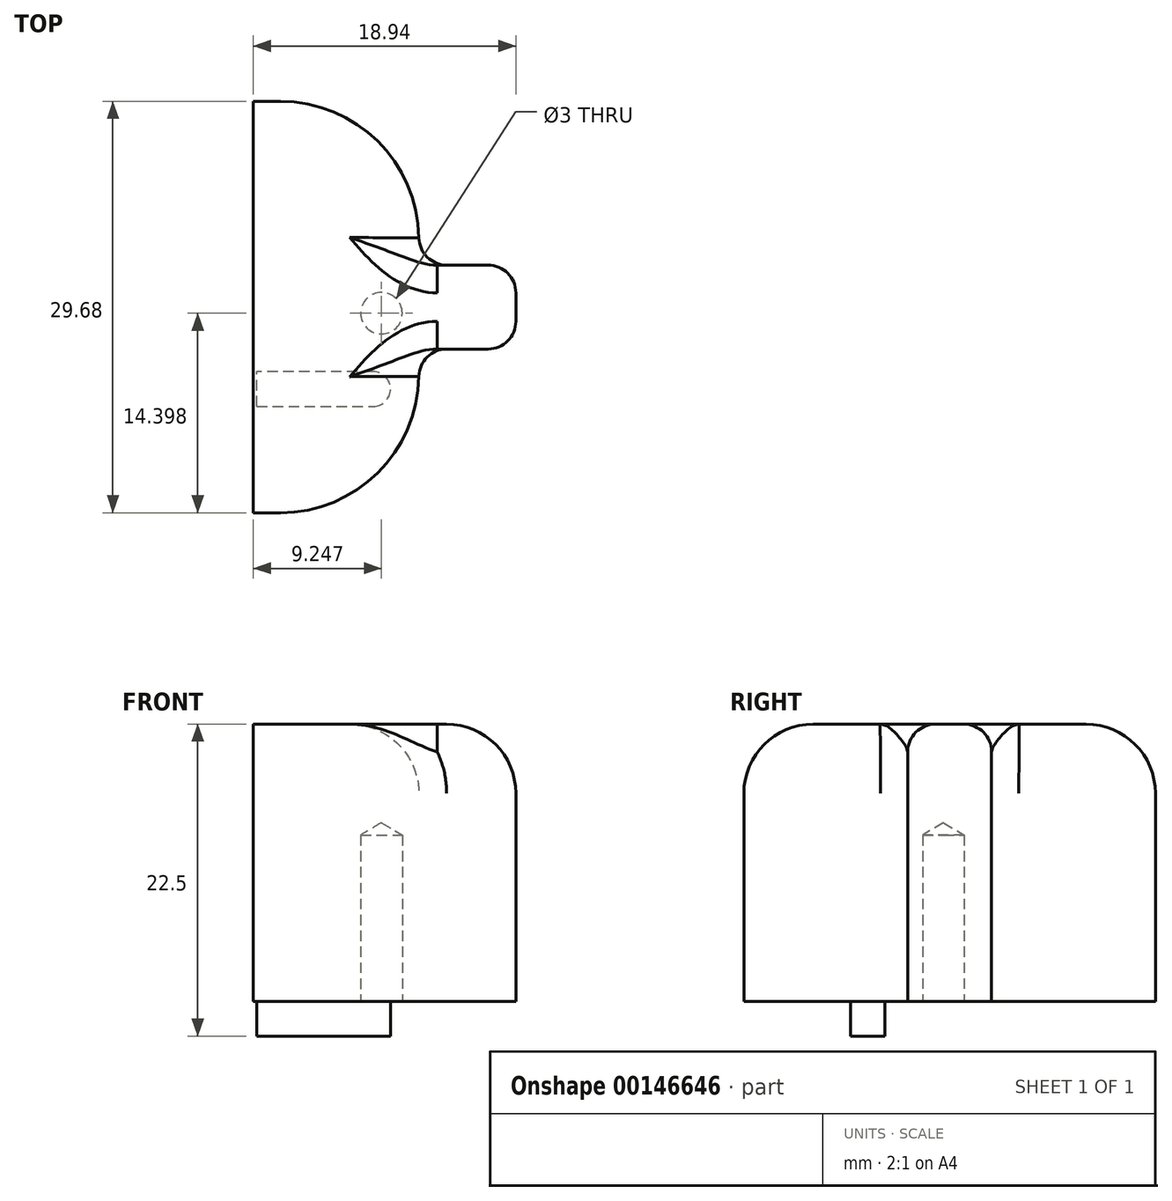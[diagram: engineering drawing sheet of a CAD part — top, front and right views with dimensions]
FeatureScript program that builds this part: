
annotation { "Feature Type Name" : "Feature", "Feature Type Description" : "" }
export const myFeature = defineFeature(function(context is Context, id is Id, definition is map)
    precondition{}
    {
        {
            var Q0;
            Q0=qCreatedBy(makeId("Top.planeOp"),FACE);
            var sketch = newSketch(context, id + "F0", { "sketchPlane" : qUnion([Q0])});
            skLineSegment(sketch, "E0.MirrorCS", {"start": v(19.51, -1.25) * mm, "end": v(19.51, 1.25) * mm});
            skLineSegment(sketch, "E1.MirrorCS", {"start": v(27.92, 1.25) * mm, "end": v(19.51, 1.25) * mm});
            skArc(sketch, "E2.MirrorCS", {"start": v(27.92, -1.25) * mm, "mid": v(29.17, 0) * mm, "end": v(27.92, 1.25) * mm});
            skLineSegment(sketch, "E3.MirrorCS", {"start": v(19.51, -1.25) * mm, "end": v(27.92, -1.25) * mm});
            skLineSegment(sketch, "E4.MirrorCS", {"start": v(19.26, -8.93) * mm, "end": v(19.26, 8.93) * mm});
            skCircle(sketch, "E5.MirrorC", {"center": v(28.5, 5.47) * mm, "radius": 1.5 * mm, "construction": true});
            skLineSegment(sketch, "E6.MirrorCS", {"start": v(38.2, 8.93) * mm, "end": v(31.21, 8.93) * mm});
            skLineSegment(sketch, "E7.MirrorCS", {"start": v(38.2, 2.88) * mm, "end": v(38.2, 8.93) * mm});
            skLineSegment(sketch, "E8.MirrorCS", {"start": v(31.21, 2.88) * mm, "end": v(38.2, 2.88) * mm});
            skLineSegment(sketch, "E9.MirrorCS", {"start": v(19.26, -8.93) * mm, "end": v(21.21, -8.93) * mm});
            skArc(sketch, "E10.MirrorCS", {"start": v(21.21, -8.93) * mm, "mid": v(28.28, -6) * mm, "end": v(31.21, 1.07) * mm});
            skLineSegment(sketch, "E11.MirrorCS", {"start": v(31.21, 1.07) * mm, "end": v(31.21, 2.88) * mm});
            skLineSegment(sketch, "E12", {"start": v(19.24, 5.9) * mm, "end": v(38.2, 5.9) * mm, "construction": true});
            skLineSegment(sketch, "E13.MirrorCS", {"start": v(31.21, 10.75) * mm, "end": v(31.21, 8.93) * mm});
            skArc(sketch, "E14.MirrorCS", {"start": v(21.21, 20.75) * mm, "mid": v(28.28, 17.82) * mm, "end": v(31.21, 10.75) * mm});
            skLineSegment(sketch, "E15.MirrorCS", {"start": v(19.26, 20.75) * mm, "end": v(21.21, 20.75) * mm});
            skLineSegment(sketch, "E16", {"start": v(19.26, 20.75) * mm, "end": v(19.26, 8.93) * mm});
            skSolve(sketch);
        }
        {
            var Q0;
            Q0=makeQuery(id+"F0.imprint","IMPRINT",FACE,{"disambiguationData":[TD([[makeQuery(id+"F0.imprint","IMPRINT",EDGE,{"derivedFrom":sQuery(id+"F0.wireOp",EDGE,"E0.MirrorCS")}),-1.0]])]});
            extrude(context, id + "F1", {"entities" : qUnion([Q0]), "oppositeDirection" : true, "depth" : 2.5 * mm});
        }
        {
            var Q0;
            Q0=makeQuery(id+"F0.imprint","IMPRINT",FACE,{"disambiguationData":[TD([[makeQuery(id+"F0.imprint","IMPRINT",EDGE,{"derivedFrom":sQuery(id+"F0.wireOp",EDGE,"E0.MirrorCS")}),1.0]])]});
            var Q1;
            Q1=makeQuery(id+"F0.imprint","IMPRINT",FACE,{"disambiguationData":[TD([[makeQuery(id+"F0.imprint","IMPRINT",EDGE,{"derivedFrom":sQuery(id+"F0.wireOp",EDGE,"E0.MirrorCS")}),-1.0]])]});
            extrude(context, id + "F2", {"entities" : qUnion([Q0, Q1]), "operationType" : NewBodyOperationType.ADD, "depth" : 20 * mm});
        }
        {
            var Q0;
            Q0=sQuery(id+"F0.wireOp",VERTEX,"E5.MirrorC.center");
            var Q1;
            Q1=makeQuery(id+"F1.opExtrude","SWEPT_BODY",BODY,{"disambiguationData":[OSD([sQuery(id+"F0.wireOp",EDGE,"E0.MirrorCS"),sQuery(id+"F0.wireOp",EDGE,"E1.MirrorCS"),sQuery(id+"F0.wireOp",EDGE,"E2.MirrorCS"),sQuery(id+"F0.wireOp",EDGE,"E3.MirrorCS")])]});
            hole(context, id + "F3", {"style" : HoleStyle.SIMPLE, "endStyle" : HoleEndStyle.BLIND, "oppositeDirection" : true, "standardTappedOrClearance" : lookupTablePath({ "standard" : "ISO", "size" : "3", "type" : "Drilled" }), "standardBlindInLast" : lookupTablePath({ "standard" : "ISO", "size" : "3", "type" : "Drilled" }), "holeDiameter" : 3 * mm, "holeDepth" : 12 * mm, "locations" : qUnion([Q0]), "scope" : qUnion([Q1])});
        }
        {
            var Q0;
            Q0=makeQuery(id+"F2.opExtrude","CAP_EDGE",EDGE,{"disambiguationData":[OSD([sQuery(id+"F0.wireOp",EDGE,"E10.MirrorCS")])],"isStart":false});
            var Q1;
            Q1=makeQuery(id+"F2.opExtrude","CAP_EDGE",EDGE,{"disambiguationData":[OSD([sQuery(id+"F0.wireOp",EDGE,"E7.MirrorCS")])],"isStart":false});
            var Q2;
            Q2=makeQuery(id+"F2.opExtrude","CAP_EDGE",EDGE,{"disambiguationData":[OSD([sQuery(id+"F0.wireOp",EDGE,"E14.MirrorCS")])],"isStart":false});
            fillet(context, id + "F4", {"entities" : qUnion([Q0, Q1, Q2]), "radius" : 5 * mm, "tangentPropagation" : true, "allowEdgeOverflow" : false});
        }
        {
            var Q0;
            Q0=makeQuery(id+"F2.opExtrude","SWEPT_EDGE",EDGE,{"disambiguationData":[OSD([sQuery(id+"F0.wireOp",EDGE,"E8.MirrorCS"),sQuery(id+"F0.wireOp",EDGE,"E11.MirrorCS")])]});
            var Q1;
            Q1=makeQuery(id+"F2.opExtrude","SWEPT_EDGE",EDGE,{"disambiguationData":[OSD([sQuery(id+"F0.wireOp",EDGE,"E7.MirrorCS"),sQuery(id+"F0.wireOp",EDGE,"E8.MirrorCS")])]});
            var Q2;
            Q2=makeQuery(id+"F2.opExtrude","SWEPT_EDGE",EDGE,{"disambiguationData":[OSD([sQuery(id+"F0.wireOp",EDGE,"E6.MirrorCS"),sQuery(id+"F0.wireOp",EDGE,"E13.MirrorCS")])]});
            var Q3;
            Q3=makeQuery(id+"F2.opExtrude","SWEPT_EDGE",EDGE,{"disambiguationData":[OSD([sQuery(id+"F0.wireOp",EDGE,"E6.MirrorCS"),sQuery(id+"F0.wireOp",EDGE,"E7.MirrorCS")])]});
            fillet(context, id + "F5", {"entities" : qUnion([Q0, Q1, Q2, Q3]), "radius" : 2 * mm, "tangentPropagation" : true, "allowEdgeOverflow" : false});
        }
    });
